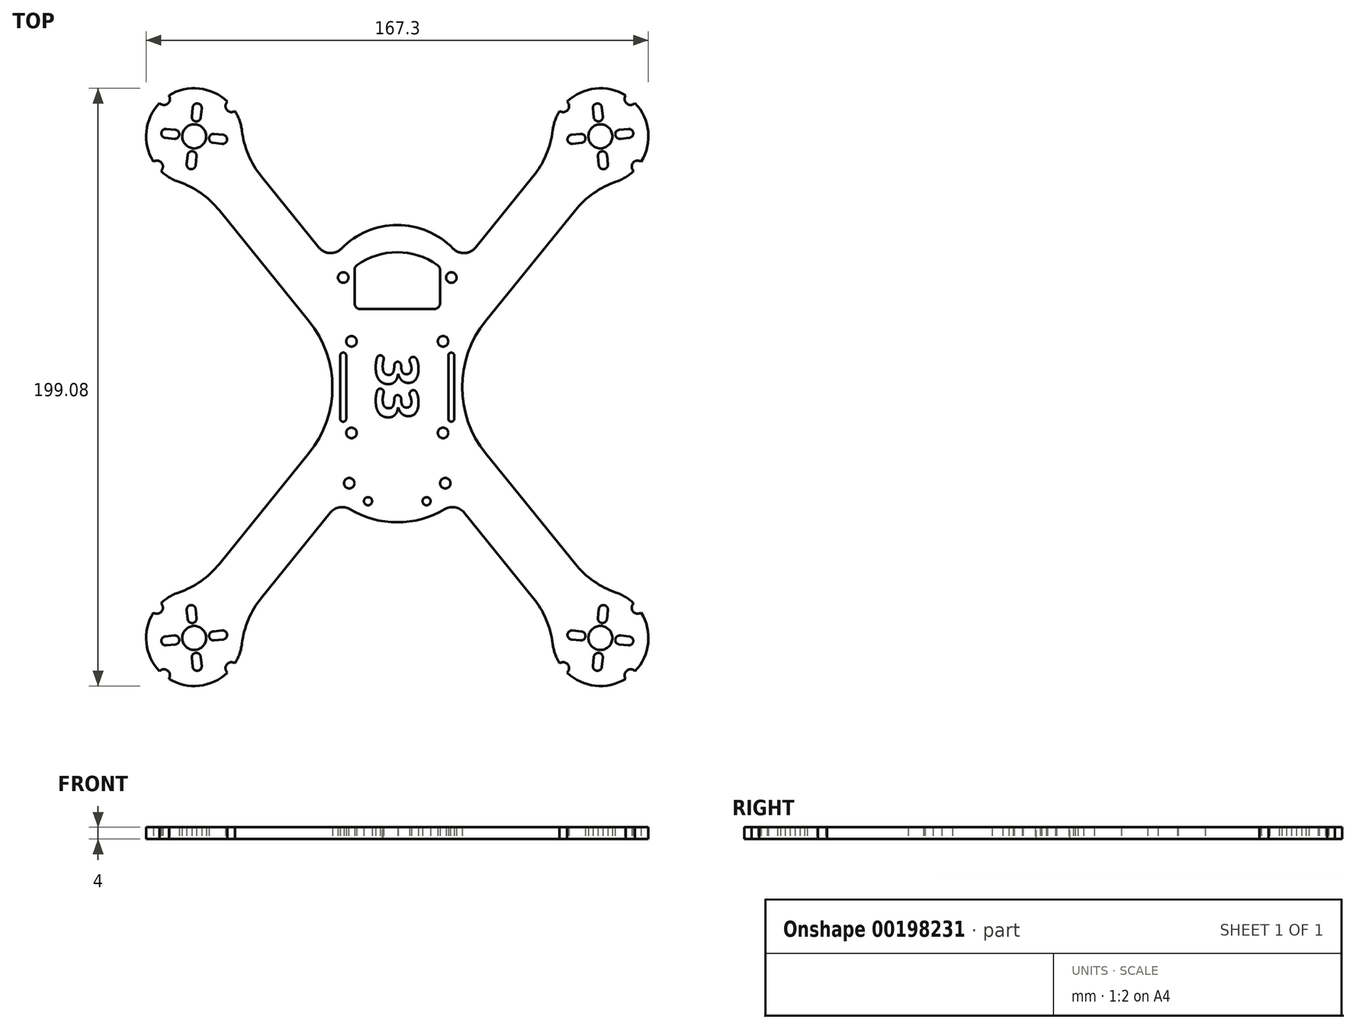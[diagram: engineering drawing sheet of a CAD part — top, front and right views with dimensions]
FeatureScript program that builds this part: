
annotation { "Feature Type Name" : "Feature", "Feature Type Description" : "" }
export const myFeature = defineFeature(function(context is Context, id is Id, definition is map)
    precondition{}
    {
        {
            var Q0;
            Q0=qCreatedBy(makeId("Top.planeOp"),FACE);
            var sketch = newSketch(context, id + "F0", { "sketchPlane" : qUnion([Q0])});
            skCircle(sketch, "E0", {"center": v(0, 0) * mm, "radius": 107.5 * mm, "construction": true});
            skCircle(sketch, "E1", {"center": v(67.65, 83.54) * mm, "radius": 63.5 * mm, "construction": true});
            skLineSegment(sketch, "E2", {"start": v(0, 0) * mm, "end": v(67.65, 83.54) * mm, "construction": true});
            skArc(sketch, "E3", {"start": v(72.85, 68.41) * mm, "mid": v(75.99, 69.89) * mm, "end": v(78.73, 72) * mm});
            skLineSegment(sketch, "E4", {"start": v(29.42, 22.03) * mm, "end": v(59.3, 58.92) * mm});
            skLineSegment(sketch, "E5", {"start": v(45.3, 70.25) * mm, "end": v(26.08, 46.5) * mm});
            skPoint(sketch, "E6.visualSharp", {"position": v(52.33, 78.93) * mm});
            skArc(sketch, "E6.filletArc", {"start": v(45.3, 70.25) * mm, "mid": v(49.61, 77.41) * mm, "end": v(51.77, 85.49) * mm});
            skPoint(sketch, "E7.visualSharp", {"position": v(66.32, 67.6) * mm});
            skArc(sketch, "E7.filletArc", {"start": v(72.85, 68.41) * mm, "mid": v(65.4, 64.62) * mm, "end": v(59.3, 58.92) * mm});
            skCircle(sketch, "E8", {"center": v(67.65, 83.54) * mm, "radius": 4 * mm});
            skLineSegment(sketch, "E9", {"start": v(0, 107.5) * mm, "end": v(0, 0) * mm, "construction": true});
            skLineSegment(sketch, "E10", {"start": v(0, 0) * mm, "end": v(107.5, 0) * mm, "construction": true});
            skArc(sketch, "E11.MirrorCS", {"start": v(-72.85, 68.41) * mm, "mid": v(-65.4, 64.62) * mm, "end": v(-59.3, 58.92) * mm});
            skArc(sketch, "E12.MirrorCS", {"start": v(-45.3, 70.25) * mm, "mid": v(-49.61, 77.41) * mm, "end": v(-51.77, 85.49) * mm});
            skPoint(sketch, "E13.MirrorP", {"position": v(-66.32, 67.6) * mm});
            skPoint(sketch, "E14.MirrorP", {"position": v(-52.33, 78.93) * mm});
            skArc(sketch, "E15.MirrorCS", {"start": v(-72.85, 68.41) * mm, "mid": v(-75.99, 69.89) * mm, "end": v(-78.73, 72) * mm});
            skLineSegment(sketch, "E16.MirrorCS", {"start": v(-29.42, 22.03) * mm, "end": v(-59.3, 58.92) * mm});
            skLineSegment(sketch, "E17.MirrorCS", {"start": v(-45.3, 70.25) * mm, "end": v(-26.08, 46.5) * mm});
            skCircle(sketch, "E18.MirrorC", {"center": v(-67.65, 83.54) * mm, "radius": 4 * mm});
            skCircle(sketch, "E19.MirrorC", {"center": v(-67.65, 83.54) * mm, "radius": 63.5 * mm, "construction": true});
            skLineSegment(sketch, "E20.MirrorCS", {"start": v(0, 0) * mm, "end": v(-67.65, 83.54) * mm, "construction": true});
            skArc(sketch, "E21.MirrorCS", {"start": v(-72.85, -68.41) * mm, "mid": v(-65.4, -64.62) * mm, "end": v(-59.3, -58.92) * mm});
            skArc(sketch, "E22.MirrorCS", {"start": v(-45.3, -70.25) * mm, "mid": v(-49.61, -77.41) * mm, "end": v(-51.77, -85.49) * mm});
            skPoint(sketch, "E23.MirrorP", {"position": v(-52.33, -78.93) * mm});
            skArc(sketch, "E24.MirrorCS", {"start": v(-72.85, -68.41) * mm, "mid": v(-75.99, -69.89) * mm, "end": v(-78.73, -72) * mm});
            skPoint(sketch, "E25.MirrorP", {"position": v(-66.32, -67.6) * mm});
            skCircle(sketch, "E26.MirrorC", {"center": v(-67.65, -83.54) * mm, "radius": 4 * mm});
            skLineSegment(sketch, "E27.MirrorCS", {"start": v(-29.42, -22.03) * mm, "end": v(-59.3, -58.92) * mm});
            skArc(sketch, "E28.MirrorCS", {"start": v(45.3, -70.25) * mm, "mid": v(49.61, -77.41) * mm, "end": v(51.77, -85.49) * mm});
            skArc(sketch, "E29.MirrorCS", {"start": v(72.85, -68.41) * mm, "mid": v(65.4, -64.62) * mm, "end": v(59.3, -58.92) * mm});
            skCircle(sketch, "E30.MirrorC", {"center": v(67.65, -83.54) * mm, "radius": 4 * mm});
            skPoint(sketch, "E31.MirrorP", {"position": v(66.32, -67.6) * mm});
            skArc(sketch, "E32.MirrorCS", {"start": v(72.85, -68.41) * mm, "mid": v(75.99, -69.89) * mm, "end": v(78.73, -72) * mm});
            skPoint(sketch, "E33.MirrorP", {"position": v(52.33, -78.93) * mm});
            skCircle(sketch, "E34.MirrorC", {"center": v(67.65, -83.54) * mm, "radius": 63.5 * mm, "construction": true});
            skCircle(sketch, "E35.MirrorC", {"center": v(-67.65, -83.54) * mm, "radius": 63.5 * mm, "construction": true});
            skLineSegment(sketch, "E36.MirrorCS", {"start": v(29.42, -22.03) * mm, "end": v(59.3, -58.92) * mm});
            skLineSegment(sketch, "E37.MirrorCS", {"start": v(0, 0) * mm, "end": v(-67.65, -83.54) * mm, "construction": true});
            skLineSegment(sketch, "E38.MirrorCS", {"start": v(0, 0) * mm, "end": v(67.65, -83.54) * mm, "construction": true});
            skCircle(sketch, "E39", {"center": v(-15.25, -15.25) * mm, "radius": 1.75 * mm});
            skCircle(sketch, "E40", {"center": v(15.25, -15.25) * mm, "radius": 1.75 * mm});
            skCircle(sketch, "E41.MirrorC", {"center": v(15.25, 15.25) * mm, "radius": 1.75 * mm});
            skCircle(sketch, "E42.MirrorC", {"center": v(-15.25, 15.25) * mm, "radius": 1.75 * mm});
            skLineSegment(sketch, "E43", {"start": v(-12.25, 26) * mm, "end": v(12.25, 26) * mm});
            skLineSegment(sketch, "E44", {"start": v(-14.25, 28) * mm, "end": v(-14.25, 39) * mm});
            skLineSegment(sketch, "E45", {"start": v(14.25, 28) * mm, "end": v(14.25, 39) * mm});
            skArc(sketch, "E46", {"start": v(18.61, 46.16) * mm, "mid": v(0, 54) * mm, "end": v(-18.61, 46.16) * mm});
            skPoint(sketch, "E47.visualSharp", {"position": v(-22.14, 41.64) * mm});
            skArc(sketch, "E47.filletArc", {"start": v(-26.08, 46.5) * mm, "mid": v(-22.42, 44.65) * mm, "end": v(-18.61, 46.16) * mm});
            skPoint(sketch, "E48.visualSharp", {"position": v(22.14, 41.64) * mm});
            skArc(sketch, "E48.filletArc", {"start": v(18.61, 46.16) * mm, "mid": v(22.42, 44.65) * mm, "end": v(26.08, 46.5) * mm});
            skPoint(sketch, "E49.visualSharp", {"position": v(-14.25, 26) * mm});
            skArc(sketch, "E49.filletArc", {"start": v(-14.25, 28) * mm, "mid": v(-13.66, 26.59) * mm, "end": v(-12.25, 26) * mm});
            skPoint(sketch, "E50.visualSharp", {"position": v(14.25, 26) * mm});
            skArc(sketch, "E50.filletArc", {"start": v(12.25, 26) * mm, "mid": v(13.66, 26.59) * mm, "end": v(14.25, 28) * mm});
            skPoint(sketch, "E51.visualSharp", {"position": v(-14.25, 40) * mm});
            skPoint(sketch, "E52.visualSharp", {"position": v(14.25, 44) * mm});
            skArc(sketch, "E53", {"start": v(-29.42, -22.03) * mm, "mid": v(-21.62, 0) * mm, "end": v(-29.42, 22.03) * mm});
            skArc(sketch, "E54.MirrorCS", {"start": v(29.42, -22.03) * mm, "mid": v(21.62, 0) * mm, "end": v(29.42, 22.03) * mm});
            skLineSegment(sketch, "E55", {"start": v(-45.3, -70.25) * mm, "end": v(-22.27, -41.8) * mm});
            skLineSegment(sketch, "E56", {"start": v(45.3, -70.25) * mm, "end": v(22.27, -41.8) * mm});
            skCircle(sketch, "E57", {"center": v(-16, -32) * mm, "radius": 1.75 * mm});
            skCircle(sketch, "E58.MirrorC", {"center": v(16, -32) * mm, "radius": 1.75 * mm});
            skCircle(sketch, "E59", {"center": v(-18, 36.5) * mm, "radius": 1.75 * mm});
            skCircle(sketch, "E60.MirrorC", {"center": v(18, 36.5) * mm, "radius": 1.75 * mm});
            skLineSegment(sketch, "E61.bottom", {"start": v(-19, 10.5) * mm, "end": v(-17, 10.5) * mm, "construction": true});
            skLineSegment(sketch, "E61.top", {"start": v(-19, -10.5) * mm, "end": v(-17, -10.5) * mm, "construction": true});
            skLineSegment(sketch, "E61.left", {"start": v(-19, 10.5) * mm, "end": v(-19, -10.5) * mm});
            skLineSegment(sketch, "E61.right", {"start": v(-17, 10.5) * mm, "end": v(-17, -10.5) * mm});
            skArc(sketch, "E62", {"start": v(-17, 10.5) * mm, "mid": v(-18, 11.5) * mm, "end": v(-19, 10.5) * mm});
            skArc(sketch, "E63", {"start": v(-19, -10.5) * mm, "mid": v(-18, -11.5) * mm, "end": v(-17, -10.5) * mm});
            skArc(sketch, "E64.MirrorCS", {"start": v(19, -10.5) * mm, "mid": v(18, -11.5) * mm, "end": v(17, -10.5) * mm});
            skLineSegment(sketch, "E65.MirrorCS", {"start": v(19, 10.5) * mm, "end": v(17, 10.5) * mm, "construction": true});
            skLineSegment(sketch, "E66.MirrorCS", {"start": v(19, -10.5) * mm, "end": v(17, -10.5) * mm, "construction": true});
            skLineSegment(sketch, "E67.MirrorCS", {"start": v(19, 10.5) * mm, "end": v(19, -10.5) * mm});
            skLineSegment(sketch, "E68.MirrorCS", {"start": v(17, 10.5) * mm, "end": v(17, -10.5) * mm});
            skArc(sketch, "E69.MirrorCS", {"start": v(17, 10.5) * mm, "mid": v(18, 11.5) * mm, "end": v(19, 10.5) * mm});
            skArc(sketch, "E70", {"start": v(-76.1, -97.14) * mm, "mid": v(-76.46, -94.42) * mm, "end": v(-79.2, -94.62) * mm});
            skArc(sketch, "E71", {"start": v(-81.25, -75.1) * mm, "mid": v(-78.53, -74.73) * mm, "end": v(-78.73, -72) * mm});
            skArc(sketch, "E72", {"start": v(-54.06, -91.98) * mm, "mid": v(-56.77, -92.35) * mm, "end": v(-56.57, -95.08) * mm});
            skLineSegment(sketch, "E73", {"start": v(-80.09, -73.47) * mm, "end": v(-55.22, -93.61) * mm, "construction": true});
            skArc(sketch, "E74.MirrorC", {"start": v(76.1, -97.14) * mm, "mid": v(76.46, -94.42) * mm, "end": v(79.2, -94.62) * mm});
            skArc(sketch, "E75.MirrorC", {"start": v(81.25, -75.1) * mm, "mid": v(78.53, -74.73) * mm, "end": v(78.73, -72) * mm});
            skArc(sketch, "E76.MirrorC", {"start": v(54.06, -91.98) * mm, "mid": v(56.77, -92.35) * mm, "end": v(56.57, -95.08) * mm});
            skArc(sketch, "E77.MirrorC", {"start": v(-81.25, 75.1) * mm, "mid": v(-78.53, 74.73) * mm, "end": v(-78.73, 72) * mm});
            skArc(sketch, "E78.MirrorC", {"start": v(-76.1, 97.14) * mm, "mid": v(-76.46, 94.42) * mm, "end": v(-79.2, 94.62) * mm});
            skArc(sketch, "E79.MirrorC", {"start": v(-54.06, 91.98) * mm, "mid": v(-56.77, 92.35) * mm, "end": v(-56.57, 95.08) * mm});
            skArc(sketch, "E80.MirrorC", {"start": v(81.25, 75.1) * mm, "mid": v(78.53, 74.73) * mm, "end": v(78.73, 72) * mm});
            skArc(sketch, "E81.MirrorC", {"start": v(76.1, 97.14) * mm, "mid": v(76.46, 94.42) * mm, "end": v(79.2, 94.62) * mm});
            skArc(sketch, "E82.MirrorC", {"start": v(54.06, 91.98) * mm, "mid": v(56.77, 92.35) * mm, "end": v(56.57, 95.08) * mm});
            skArc(sketch, "E83.trimOffspring", {"start": v(-76.1, 97.14) * mm, "mid": v(-65.98, 99.46) * mm, "end": v(-56.57, 95.08) * mm});
            skArc(sketch, "E84.trimOffspring", {"start": v(-81.25, 75.1) * mm, "mid": v(-83.56, 85.22) * mm, "end": v(-79.2, 94.62) * mm});
            skArc(sketch, "E85.trimOffspring", {"start": v(-54.06, 91.98) * mm, "mid": v(-52.56, 88.86) * mm, "end": v(-51.77, 85.49) * mm});
            skArc(sketch, "E86.trimOffspring", {"start": v(76.1, 97.14) * mm, "mid": v(65.98, 99.46) * mm, "end": v(56.57, 95.08) * mm});
            skArc(sketch, "E87.trimOffspring", {"start": v(54.06, 91.98) * mm, "mid": v(52.56, 88.86) * mm, "end": v(51.77, 85.49) * mm});
            skArc(sketch, "E88.trimOffspring", {"start": v(81.25, 75.1) * mm, "mid": v(83.56, 85.22) * mm, "end": v(79.2, 94.62) * mm});
            skArc(sketch, "E89.trimOffspring", {"start": v(-54.5, -92.66) * mm, "mid": v(-52.7, -89.24) * mm, "end": v(-51.77, -85.49) * mm});
            skArc(sketch, "E90.trimOffspring", {"start": v(-76.1, -97.14) * mm, "mid": v(-65.98, -99.46) * mm, "end": v(-56.57, -95.08) * mm});
            skLineSegment(sketch, "E91", {"start": v(-67.65, -83.54) * mm, "end": v(-77.72, -95.98) * mm, "construction": true});
            skArc(sketch, "E92.trimOffspring", {"start": v(-81.25, -75.1) * mm, "mid": v(-83.56, -85.22) * mm, "end": v(-79.2, -94.62) * mm});
            skArc(sketch, "E93.trimOffspring", {"start": v(81.25, -75.1) * mm, "mid": v(83.56, -85.22) * mm, "end": v(79.2, -94.62) * mm});
            skArc(sketch, "E94.trimOffspring", {"start": v(54.06, -91.98) * mm, "mid": v(52.56, -88.86) * mm, "end": v(51.77, -85.49) * mm});
            skArc(sketch, "E95.trimOffspring", {"start": v(76.1, -97.14) * mm, "mid": v(65.98, -99.46) * mm, "end": v(56.57, -95.08) * mm});
            skArc(sketch, "E96", {"start": v(13.42, 40.63) * mm, "mid": v(0, 44.95) * mm, "end": v(-13.42, 40.63) * mm});
            skArc(sketch, "E97.filletArc", {"start": v(-13.42, 40.63) * mm, "mid": v(-14.03, 39.92) * mm, "end": v(-14.25, 39) * mm});
            skPoint(sketch, "E98.visualSharp", {"position": v(14.25, 40) * mm});
            skArc(sketch, "E98.filletArc", {"start": v(14.25, 39) * mm, "mid": v(14.03, 39.92) * mm, "end": v(13.42, 40.63) * mm});
            skLineSegment(sketch, "E99", {"start": v(67.65, -83.54) * mm, "end": v(69.32, -67.63) * mm, "construction": true});
            skArc(sketch, "E100", {"start": v(66.84, -76.92) * mm, "mid": v(68.17, -78.57) * mm, "end": v(69.82, -77.24) * mm});
            skArc(sketch, "E101", {"start": v(70.14, -74.25) * mm, "mid": v(68.8, -72.6) * mm, "end": v(67.15, -73.94) * mm});
            skLineSegment(sketch, "E102", {"start": v(69.82, -77.24) * mm, "end": v(70.14, -74.25) * mm});
            skLineSegment(sketch, "E103", {"start": v(66.84, -76.92) * mm, "end": v(67.15, -73.94) * mm});
            skArc(sketch, "E104.1.0", {"start": v(61.03, -84.36) * mm, "mid": v(62.68, -83.02) * mm, "end": v(61.34, -81.37) * mm});
            skLineSegment(sketch, "E104.1.1", {"start": v(61.03, -84.36) * mm, "end": v(58.05, -84.04) * mm});
            skArc(sketch, "E104.1.2", {"start": v(58.36, -81.06) * mm, "mid": v(56.71, -82.4) * mm, "end": v(58.05, -84.04) * mm});
            skLineSegment(sketch, "E104.1.3", {"start": v(61.34, -81.37) * mm, "end": v(58.36, -81.06) * mm});
            skLineSegment(sketch, "E104.1.4", {"start": v(67.65, -83.54) * mm, "end": v(51.74, -81.87) * mm, "construction": true});
            skArc(sketch, "E104.2.0", {"start": v(68.46, -90.16) * mm, "mid": v(67.13, -88.52) * mm, "end": v(65.48, -89.85) * mm});
            skLineSegment(sketch, "E104.2.1", {"start": v(68.46, -90.16) * mm, "end": v(68.15, -93.15) * mm});
            skArc(sketch, "E104.2.2", {"start": v(65.17, -92.83) * mm, "mid": v(66.5, -94.48) * mm, "end": v(68.15, -93.15) * mm});
            skLineSegment(sketch, "E104.2.3", {"start": v(65.48, -89.85) * mm, "end": v(65.17, -92.83) * mm});
            skLineSegment(sketch, "E104.2.4", {"start": v(67.65, -83.54) * mm, "end": v(65.98, -99.46) * mm, "construction": true});
            skArc(sketch, "E104.3.0", {"start": v(74.27, -82.73) * mm, "mid": v(72.62, -84.07) * mm, "end": v(73.96, -85.71) * mm});
            skLineSegment(sketch, "E104.3.1", {"start": v(74.27, -82.73) * mm, "end": v(77.26, -83.04) * mm});
            skArc(sketch, "E104.3.2", {"start": v(76.94, -86.03) * mm, "mid": v(78.6, -84.7) * mm, "end": v(77.26, -83.04) * mm});
            skLineSegment(sketch, "E104.3.3", {"start": v(73.96, -85.71) * mm, "end": v(76.94, -86.03) * mm});
            skLineSegment(sketch, "E104.3.4", {"start": v(67.65, -83.54) * mm, "end": v(83.56, -85.22) * mm, "construction": true});
            skLineSegment(sketch, "E105.MirrorCS", {"start": v(-68.46, -90.16) * mm, "end": v(-68.15, -93.15) * mm});
            skArc(sketch, "E106.MirrorCS", {"start": v(-68.46, -90.16) * mm, "mid": v(-67.13, -88.52) * mm, "end": v(-65.48, -89.85) * mm});
            skLineSegment(sketch, "E107.MirrorCS", {"start": v(-65.48, -89.85) * mm, "end": v(-65.17, -92.83) * mm});
            skArc(sketch, "E108.MirrorCS", {"start": v(-65.17, -92.83) * mm, "mid": v(-66.5, -94.48) * mm, "end": v(-68.15, -93.15) * mm});
            skLineSegment(sketch, "E109.MirrorCS", {"start": v(-67.65, -83.54) * mm, "end": v(-65.98, -99.46) * mm, "construction": true});
            skLineSegment(sketch, "E110.MirrorCS", {"start": v(-67.65, -83.54) * mm, "end": v(-83.56, -85.22) * mm, "construction": true});
            skLineSegment(sketch, "E111.MirrorCS", {"start": v(-67.65, -83.54) * mm, "end": v(-51.74, -81.87) * mm, "construction": true});
            skLineSegment(sketch, "E112.MirrorCS", {"start": v(-67.65, -83.54) * mm, "end": v(-69.32, -67.63) * mm, "construction": true});
            skLineSegment(sketch, "E113.MirrorCS", {"start": v(-69.82, -77.24) * mm, "end": v(-70.14, -74.25) * mm});
            skLineSegment(sketch, "E114.MirrorCS", {"start": v(-66.84, -76.92) * mm, "end": v(-67.15, -73.94) * mm});
            skArc(sketch, "E115.MirrorCS", {"start": v(-70.14, -74.25) * mm, "mid": v(-68.8, -72.6) * mm, "end": v(-67.15, -73.94) * mm});
            skArc(sketch, "E116.MirrorCS", {"start": v(-66.84, -76.92) * mm, "mid": v(-68.17, -78.57) * mm, "end": v(-69.82, -77.24) * mm});
            skLineSegment(sketch, "E117.MirrorCS", {"start": v(-74.27, -82.73) * mm, "end": v(-77.26, -83.04) * mm});
            skArc(sketch, "E118.MirrorCS", {"start": v(-76.94, -86.03) * mm, "mid": v(-78.6, -84.7) * mm, "end": v(-77.26, -83.04) * mm});
            skLineSegment(sketch, "E119.MirrorCS", {"start": v(-73.96, -85.71) * mm, "end": v(-76.94, -86.03) * mm});
            skArc(sketch, "E120.MirrorCS", {"start": v(-74.27, -82.73) * mm, "mid": v(-72.62, -84.07) * mm, "end": v(-73.96, -85.71) * mm});
            skLineSegment(sketch, "E121.MirrorCS", {"start": v(-61.03, -84.36) * mm, "end": v(-58.05, -84.04) * mm});
            skArc(sketch, "E122.MirrorCS", {"start": v(-58.36, -81.06) * mm, "mid": v(-56.71, -82.4) * mm, "end": v(-58.05, -84.04) * mm});
            skLineSegment(sketch, "E123.MirrorCS", {"start": v(-61.34, -81.37) * mm, "end": v(-58.36, -81.06) * mm});
            skArc(sketch, "E124.MirrorCS", {"start": v(-61.03, -84.36) * mm, "mid": v(-62.68, -83.02) * mm, "end": v(-61.34, -81.37) * mm});
            skArc(sketch, "E125.MirrorCS", {"start": v(-74.27, 82.73) * mm, "mid": v(-72.62, 84.07) * mm, "end": v(-73.96, 85.71) * mm});
            skLineSegment(sketch, "E126.MirrorCS", {"start": v(-73.96, 85.71) * mm, "end": v(-76.94, 86.03) * mm});
            skArc(sketch, "E127.MirrorCS", {"start": v(-76.94, 86.03) * mm, "mid": v(-78.6, 84.7) * mm, "end": v(-77.26, 83.04) * mm});
            skLineSegment(sketch, "E128.MirrorCS", {"start": v(-74.27, 82.73) * mm, "end": v(-77.26, 83.04) * mm});
            skLineSegment(sketch, "E129.MirrorCS", {"start": v(-67.65, 83.54) * mm, "end": v(-83.56, 85.22) * mm, "construction": true});
            skLineSegment(sketch, "E130.MirrorCS", {"start": v(-67.65, 83.54) * mm, "end": v(-69.32, 67.63) * mm, "construction": true});
            skLineSegment(sketch, "E131.MirrorCS", {"start": v(-67.65, 83.54) * mm, "end": v(-51.74, 81.87) * mm, "construction": true});
            skLineSegment(sketch, "E132.MirrorCS", {"start": v(-67.65, 83.54) * mm, "end": v(-65.98, 99.46) * mm, "construction": true});
            skArc(sketch, "E133.MirrorCS", {"start": v(-66.84, 76.92) * mm, "mid": v(-68.17, 78.57) * mm, "end": v(-69.82, 77.24) * mm});
            skLineSegment(sketch, "E134.MirrorCS", {"start": v(-69.82, 77.24) * mm, "end": v(-70.14, 74.25) * mm});
            skLineSegment(sketch, "E135.MirrorCS", {"start": v(-66.84, 76.92) * mm, "end": v(-67.15, 73.94) * mm});
            skArc(sketch, "E136.MirrorCS", {"start": v(-70.14, 74.25) * mm, "mid": v(-68.8, 72.6) * mm, "end": v(-67.15, 73.94) * mm});
            skArc(sketch, "E137.MirrorCS", {"start": v(-61.03, 84.36) * mm, "mid": v(-62.68, 83.02) * mm, "end": v(-61.34, 81.37) * mm});
            skLineSegment(sketch, "E138.MirrorCS", {"start": v(-61.03, 84.36) * mm, "end": v(-58.05, 84.04) * mm});
            skLineSegment(sketch, "E139.MirrorCS", {"start": v(-61.34, 81.37) * mm, "end": v(-58.36, 81.06) * mm});
            skArc(sketch, "E140.MirrorCS", {"start": v(-58.36, 81.06) * mm, "mid": v(-56.71, 82.4) * mm, "end": v(-58.05, 84.04) * mm});
            skLineSegment(sketch, "E141.MirrorCS", {"start": v(-68.46, 90.16) * mm, "end": v(-68.15, 93.15) * mm});
            skArc(sketch, "E142.MirrorCS", {"start": v(-65.17, 92.83) * mm, "mid": v(-66.5, 94.48) * mm, "end": v(-68.15, 93.15) * mm});
            skLineSegment(sketch, "E143.MirrorCS", {"start": v(-65.48, 89.85) * mm, "end": v(-65.17, 92.83) * mm});
            skArc(sketch, "E144.MirrorCS", {"start": v(-68.46, 90.16) * mm, "mid": v(-67.13, 88.52) * mm, "end": v(-65.48, 89.85) * mm});
            skLineSegment(sketch, "E145.MirrorCS", {"start": v(65.48, 89.85) * mm, "end": v(65.17, 92.83) * mm});
            skArc(sketch, "E146.MirrorCS", {"start": v(65.17, 92.83) * mm, "mid": v(66.5, 94.48) * mm, "end": v(68.15, 93.15) * mm});
            skLineSegment(sketch, "E147.MirrorCS", {"start": v(68.46, 90.16) * mm, "end": v(68.15, 93.15) * mm});
            skArc(sketch, "E148.MirrorCS", {"start": v(68.46, 90.16) * mm, "mid": v(67.13, 88.52) * mm, "end": v(65.48, 89.85) * mm});
            skLineSegment(sketch, "E149.MirrorCS", {"start": v(74.27, 82.73) * mm, "end": v(77.26, 83.04) * mm});
            skArc(sketch, "E150.MirrorCS", {"start": v(76.94, 86.03) * mm, "mid": v(78.6, 84.7) * mm, "end": v(77.26, 83.04) * mm});
            skArc(sketch, "E151.MirrorCS", {"start": v(74.27, 82.73) * mm, "mid": v(72.62, 84.07) * mm, "end": v(73.96, 85.71) * mm});
            skLineSegment(sketch, "E152.MirrorCS", {"start": v(73.96, 85.71) * mm, "end": v(76.94, 86.03) * mm});
            skLineSegment(sketch, "E153.MirrorCS", {"start": v(69.82, 77.24) * mm, "end": v(70.14, 74.25) * mm});
            skArc(sketch, "E154.MirrorCS", {"start": v(70.14, 74.25) * mm, "mid": v(68.8, 72.6) * mm, "end": v(67.15, 73.94) * mm});
            skLineSegment(sketch, "E155.MirrorCS", {"start": v(67.65, 83.54) * mm, "end": v(69.32, 67.63) * mm, "construction": true});
            skLineSegment(sketch, "E156.MirrorCS", {"start": v(66.84, 76.92) * mm, "end": v(67.15, 73.94) * mm});
            skArc(sketch, "E157.MirrorCS", {"start": v(66.84, 76.92) * mm, "mid": v(68.17, 78.57) * mm, "end": v(69.82, 77.24) * mm});
            skArc(sketch, "E158.MirrorCS", {"start": v(58.36, 81.06) * mm, "mid": v(56.71, 82.4) * mm, "end": v(58.05, 84.04) * mm});
            skLineSegment(sketch, "E159.MirrorCS", {"start": v(61.34, 81.37) * mm, "end": v(58.36, 81.06) * mm});
            skLineSegment(sketch, "E160.MirrorCS", {"start": v(61.03, 84.36) * mm, "end": v(58.05, 84.04) * mm});
            skArc(sketch, "E161.MirrorCS", {"start": v(61.03, 84.36) * mm, "mid": v(62.68, 83.02) * mm, "end": v(61.34, 81.37) * mm});
            skLineSegment(sketch, "E162.MirrorCS", {"start": v(67.65, 83.54) * mm, "end": v(83.56, 85.22) * mm, "construction": true});
            skLineSegment(sketch, "E163.MirrorCS", {"start": v(67.65, 83.54) * mm, "end": v(65.98, 99.46) * mm, "construction": true});
            skLineSegment(sketch, "E164.MirrorCS", {"start": v(67.65, 83.54) * mm, "end": v(51.74, 81.87) * mm, "construction": true});
            skCircle(sketch, "E165", {"center": v(16, -32) * mm, "radius": 2.5 * mm, "construction": true});
            skArc(sketch, "E166.trimOffspring", {"start": v(-15.83, -40.65) * mm, "mid": v(0, -45) * mm, "end": v(15.83, -40.65) * mm});
            skPoint(sketch, "E167.visualSharp", {"position": v(-4.3, -19.62) * mm});
            skPoint(sketch, "E168.MirrorP", {"position": v(4.3, -19.62) * mm});
            skCircle(sketch, "E169", {"center": v(-9.75, -38) * mm, "radius": 1.35 * mm});
            skCircle(sketch, "E170.MirrorC", {"center": v(9.75, -38) * mm, "radius": 1.35 * mm});
            skCircle(sketch, "E171", {"center": v(9.75, -38) * mm, "radius": 2.75 * mm, "construction": true});
            skText(sketch, "E172", { "text": "33", "fontName": "OpenSans-Bold.ttf"});
            skPoint(sketch, "E173.visualSharp", {"position": v(-19.36, -38.21) * mm});
            skArc(sketch, "E173.filletArc", {"start": v(-15.83, -40.65) * mm, "mid": v(-19.27, -40.03) * mm, "end": v(-22.27, -41.8) * mm});
            skPoint(sketch, "E174.visualSharp", {"position": v(19.36, -38.21) * mm});
            skArc(sketch, "E174.filletArc", {"start": v(22.27, -41.8) * mm, "mid": v(19.27, -40.03) * mm, "end": v(15.83, -40.65) * mm});
            const initialGuessF0  = {"E172": [-0.007, 0.01135, 0, -1, 0.014]};
            skSetInitialGuess(sketch, initialGuessF0);
            skSolve(sketch);
        }
        {
            var Q0;
            Q0=qSketchRegion(id+"F0",true);
            extrude(context, id + "F1", {"entities" : qUnion([Q0]), "depth" : 4 * mm});
        }
        {
            var Q0;
            Q0=makeQuery(id+"F1.opExtrude","SWEPT_EDGE",EDGE,{"disambiguationData":[OSD([sQuery(id+"F0.wireOp",EDGE,"E172.sketch_text.stroke-7"),sQuery(id+"F0.wireOp",EDGE,"E172.sketch_text.stroke-8")])]});
            var Q1;
            Q1=makeQuery(id+"F1.opExtrude","SWEPT_EDGE",EDGE,{"disambiguationData":[OSD([sQuery(id+"F0.wireOp",EDGE,"E172.sketch_text.stroke-8"),sQuery(id+"F0.wireOp",EDGE,"E172.sketch_text.stroke-9")])]});
            var Q2;
            Q2=makeQuery(id+"F1.opExtrude","SWEPT_EDGE",EDGE,{"disambiguationData":[OSD([sQuery(id+"F0.wireOp",EDGE,"E172.sketch_text.stroke-15"),sQuery(id+"F0.wireOp",EDGE,"E172.sketch_text.stroke-16")])]});
            var Q3;
            Q3=makeQuery(id+"F1.opExtrude","SWEPT_EDGE",EDGE,{"disambiguationData":[OSD([sQuery(id+"F0.wireOp",EDGE,"E172.sketch_text.stroke-16"),sQuery(id+"F0.wireOp",EDGE,"E172.sketch_text.stroke-17")])]});
            var Q4;
            Q4=makeQuery(id+"F1.opExtrude","SWEPT_EDGE",EDGE,{"disambiguationData":[OSD([sQuery(id+"F0.wireOp",EDGE,"E172.sketch_text.stroke-22"),sQuery(id+"F0.wireOp",EDGE,"E172.sketch_text.stroke-23")])]});
            var Q5;
            Q5=makeQuery(id+"F1.opExtrude","SWEPT_EDGE",EDGE,{"disambiguationData":[OSD([sQuery(id+"F0.wireOp",EDGE,"E172.sketch_text.stroke-23"),sQuery(id+"F0.wireOp",EDGE,"E172.sketch_text.stroke-24")])]});
            var Q6;
            Q6=makeQuery(id+"F1.opExtrude","SWEPT_EDGE",EDGE,{"disambiguationData":[OSD([sQuery(id+"F0.wireOp",EDGE,"E172.sketch_text.stroke-34"),sQuery(id+"F0.wireOp",EDGE,"E172.sketch_text.stroke-35")])]});
            var Q7;
            Q7=makeQuery(id+"F1.opExtrude","SWEPT_EDGE",EDGE,{"disambiguationData":[OSD([sQuery(id+"F0.wireOp",EDGE,"E172.sketch_text.stroke-35"),sQuery(id+"F0.wireOp",EDGE,"E172.sketch_text.stroke-36")])]});
            var Q8;
            Q8=makeQuery(id+"F1.opExtrude","SWEPT_EDGE",EDGE,{"disambiguationData":[OSD([sQuery(id+"F0.wireOp",EDGE,"E172.sketch_text.stroke-42"),sQuery(id+"F0.wireOp",EDGE,"E172.sketch_text.stroke-43")])]});
            var Q9;
            Q9=makeQuery(id+"F1.opExtrude","SWEPT_EDGE",EDGE,{"disambiguationData":[OSD([sQuery(id+"F0.wireOp",EDGE,"E172.sketch_text.stroke-43"),sQuery(id+"F0.wireOp",EDGE,"E172.sketch_text.stroke-44")])]});
            var Q10;
            Q10=makeQuery(id+"F1.opExtrude","SWEPT_EDGE",EDGE,{"disambiguationData":[OSD([sQuery(id+"F0.wireOp",EDGE,"E172.sketch_text.stroke-49"),sQuery(id+"F0.wireOp",EDGE,"E172.sketch_text.stroke-50")])]});
            var Q11;
            Q11=makeQuery(id+"F1.opExtrude","SWEPT_EDGE",EDGE,{"disambiguationData":[OSD([sQuery(id+"F0.wireOp",EDGE,"E172.sketch_text.stroke-50"),sQuery(id+"F0.wireOp",EDGE,"E172.sketch_text.stroke-51")])]});
            fillet(context, id + "F2", {"entities" : qUnion([Q0, Q1, Q2, Q3, Q4, Q5, Q6, Q7, Q8, Q9, Q10, Q11]), "radius" : 1.2 * mm, "tangentPropagation" : true, "allowEdgeOverflow" : false});
        }
    });
